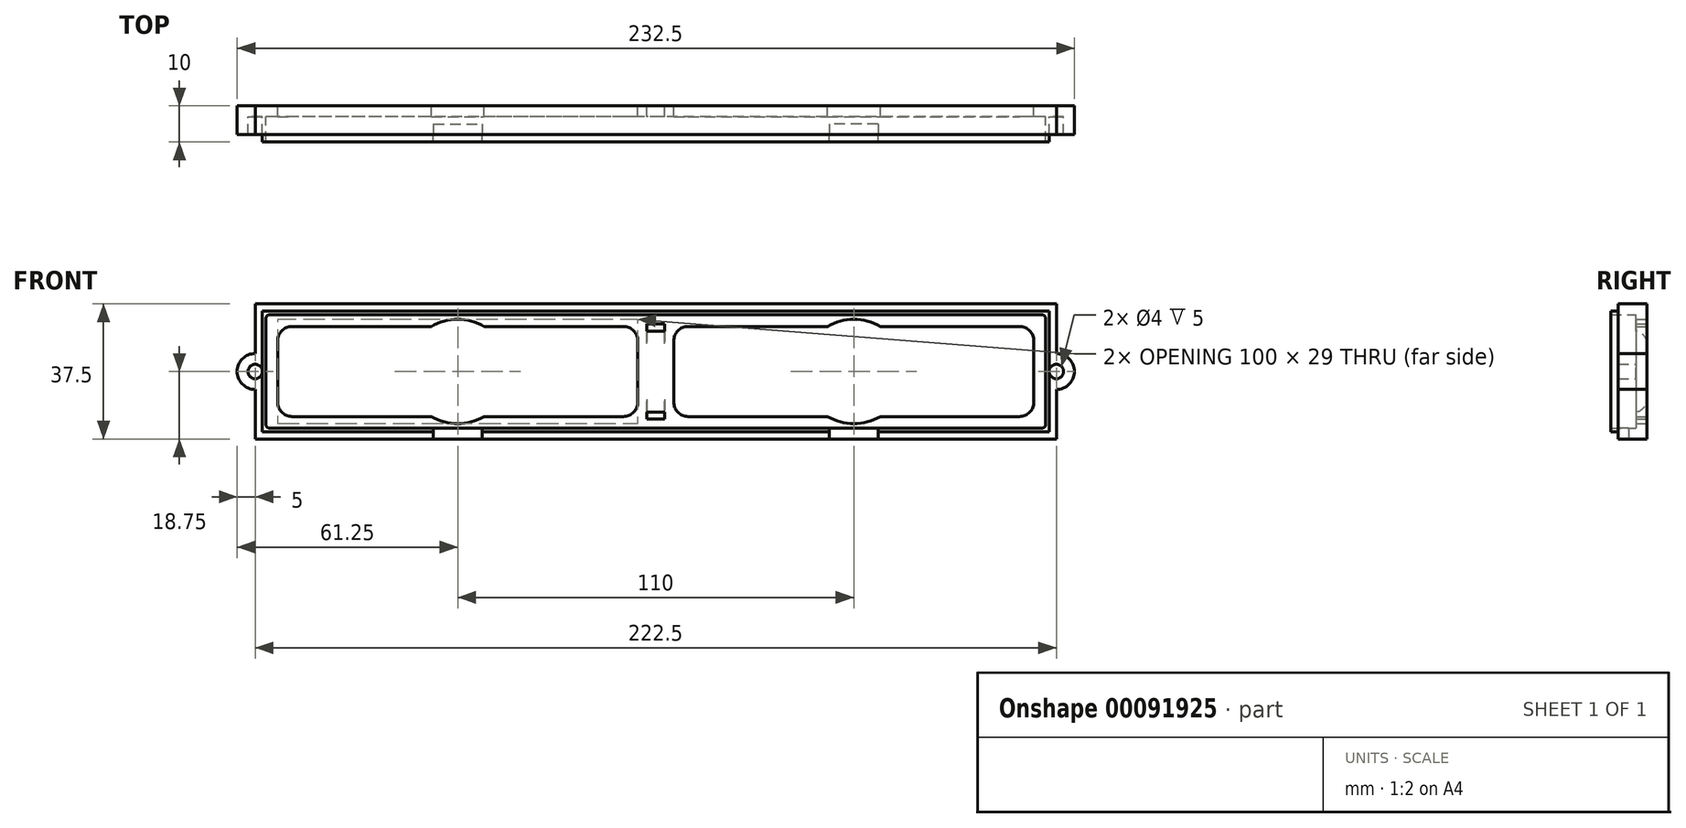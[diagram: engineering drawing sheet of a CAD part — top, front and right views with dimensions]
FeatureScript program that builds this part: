
annotation { "Feature Type Name" : "Feature", "Feature Type Description" : "" }
export const myFeature = defineFeature(function(context is Context, id is Id, definition is map)
    precondition{}
    {
        {
            var Q0;
            Q0=qCreatedBy(makeId("Front.planeOp"),FACE);
            var sketch = newSketch(context, id + "F0", { "sketchPlane" : qUnion([Q0])});
            skLineSegment(sketch, "E0.bottom", {"start": v(111.25, 18.75) * mm, "end": v(-111.25, 18.75) * mm});
            skLineSegment(sketch, "E0.top", {"start": v(111.25, -18.75) * mm, "end": v(-111.25, -18.75) * mm});
            skLineSegment(sketch, "E0.left", {"start": v(111.25, 18.75) * mm, "end": v(111.25, -18.75) * mm});
            skLineSegment(sketch, "E0.right", {"start": v(-111.25, 18.75) * mm, "end": v(-111.25, -18.75) * mm});
            skPoint(sketch, "E0.middle", {"position": v(0, 0) * mm});
            skLineSegment(sketch, "E1.bottom", {"start": v(-9, 12.5) * mm, "end": v(-101, 12.5) * mm});
            skLineSegment(sketch, "E1.top", {"start": v(-9, -12.5) * mm, "end": v(-101, -12.5) * mm});
            skLineSegment(sketch, "E1.left", {"start": v(-5, 8.5) * mm, "end": v(-5, -8.5) * mm});
            skLineSegment(sketch, "E1.right", {"start": v(-105, 8.5) * mm, "end": v(-105, -8.5) * mm});
            skPoint(sketch, "E1.middle", {"position": v(-55, 0) * mm});
            skPoint(sketch, "E2.visualSharp", {"position": v(-105, 12.5) * mm});
            skArc(sketch, "E2.filletArc", {"start": v(-101, 12.5) * mm, "mid": v(-103.83, 11.33) * mm, "end": v(-105, 8.5) * mm});
            skPoint(sketch, "E3.visualSharp", {"position": v(-5, 12.5) * mm});
            skArc(sketch, "E3.filletArc", {"start": v(-5, 8.5) * mm, "mid": v(-6.17, 11.33) * mm, "end": v(-9, 12.5) * mm});
            skPoint(sketch, "E4.visualSharp", {"position": v(-5, -12.5) * mm});
            skArc(sketch, "E4.filletArc", {"start": v(-9, -12.5) * mm, "mid": v(-6.17, -11.33) * mm, "end": v(-5, -8.5) * mm});
            skPoint(sketch, "E5.visualSharp", {"position": v(-105, -12.5) * mm});
            skArc(sketch, "E5.filletArc", {"start": v(-105, -8.5) * mm, "mid": v(-103.83, -11.33) * mm, "end": v(-101, -12.5) * mm});
            skArc(sketch, "E6.MirrorCS", {"start": v(101, 12.5) * mm, "mid": v(103.83, 11.33) * mm, "end": v(105, 8.5) * mm});
            skArc(sketch, "E7.MirrorCS", {"start": v(5, 8.5) * mm, "mid": v(6.17, 11.33) * mm, "end": v(9, 12.5) * mm});
            skArc(sketch, "E8.MirrorCS", {"start": v(9, -12.5) * mm, "mid": v(6.17, -11.33) * mm, "end": v(5, -8.5) * mm});
            skArc(sketch, "E9.MirrorCS", {"start": v(105, -8.5) * mm, "mid": v(103.83, -11.33) * mm, "end": v(101, -12.5) * mm});
            skLineSegment(sketch, "E10.MirrorCS", {"start": v(9, -12.5) * mm, "end": v(101, -12.5) * mm});
            skPoint(sketch, "E11.MirrorP", {"position": v(105, -12.5) * mm});
            skLineSegment(sketch, "E12.MirrorCS", {"start": v(5, 8.5) * mm, "end": v(5, -8.5) * mm});
            skLineSegment(sketch, "E13.MirrorCS", {"start": v(9, 12.5) * mm, "end": v(101, 12.5) * mm});
            skLineSegment(sketch, "E14.MirrorCS", {"start": v(105, 8.5) * mm, "end": v(105, -8.5) * mm});
            skPoint(sketch, "E15.MirrorP", {"position": v(5, 12.5) * mm});
            skPoint(sketch, "E16.MirrorP", {"position": v(105, 12.5) * mm});
            skPoint(sketch, "E17.MirrorP", {"position": v(55, 0) * mm});
            skPoint(sketch, "E18.MirrorP", {"position": v(5, -12.5) * mm});
            skCircle(sketch, "E19", {"center": v(-55, 0) * mm, "radius": 14.5 * mm});
            skCircle(sketch, "E20.MirrorC", {"center": v(55, 0) * mm, "radius": 14.5 * mm});
            skArc(sketch, "E21", {"start": v(-111.25, -5) * mm, "mid": v(-116.25, 0) * mm, "end": v(-111.25, 5) * mm});
            skArc(sketch, "E22.MirrorCS", {"start": v(111.25, -5) * mm, "mid": v(116.25, 0) * mm, "end": v(111.25, 5) * mm});
            skLineSegment(sketch, "E23.bottom", {"start": v(2.5, 11.25) * mm, "end": v(-2.5, 11.25) * mm});
            skLineSegment(sketch, "E23.top", {"start": v(2.5, 13.25) * mm, "end": v(-2.5, 13.25) * mm});
            skLineSegment(sketch, "E23.left", {"start": v(2.5, 11.25) * mm, "end": v(2.5, 13.25) * mm});
            skLineSegment(sketch, "E23.right", {"start": v(-2.5, 11.25) * mm, "end": v(-2.5, 13.25) * mm});
            skPoint(sketch, "E23.middle", {"position": v(0, 12.25) * mm});
            skLineSegment(sketch, "E24.MirrorCS", {"start": v(-2.5, -11.25) * mm, "end": v(-2.5, -13.25) * mm});
            skLineSegment(sketch, "E25.MirrorCS", {"start": v(2.5, -11.25) * mm, "end": v(-2.5, -11.25) * mm});
            skPoint(sketch, "E26.MirrorP", {"position": v(0, -12.25) * mm});
            skLineSegment(sketch, "E27.MirrorCS", {"start": v(2.5, -11.25) * mm, "end": v(2.5, -13.25) * mm});
            skLineSegment(sketch, "E28.MirrorCS", {"start": v(2.5, -13.25) * mm, "end": v(-2.5, -13.25) * mm});
            skSolve(sketch);
        }
        {
            var Q0;
            Q0 = qSketchRegion(id + "F0", true);
            extrude(context, id + "F1", {"entities" : qUnion([Q0]), "depth" : 3 * mm});
        }
        {
            var Q0;
            Q0=makeQuery(id+"F1.opExtrude","CAP_FACE",FACE,{"disambiguationData":[OSD([sQuery(id+"F0.wireOp",EDGE,"E0.bottom"),sQuery(id+"F0.wireOp",EDGE,"E0.top"),sQuery(id+"F0.wireOp",EDGE,"E0.left"),sQuery(id+"F0.wireOp",EDGE,"E0.right"),sQuery(id+"F0.wireOp",EDGE,"E1.bottom"),sQuery(id+"F0.wireOp",EDGE,"E1.top"),sQuery(id+"F0.wireOp",EDGE,"E1.left"),sQuery(id+"F0.wireOp",EDGE,"E1.right"),sQuery(id+"F0.wireOp",EDGE,"E2.filletArc"),sQuery(id+"F0.wireOp",EDGE,"E3.filletArc"),sQuery(id+"F0.wireOp",EDGE,"E4.filletArc"),sQuery(id+"F0.wireOp",EDGE,"E5.filletArc"),sQuery(id+"F0.wireOp",EDGE,"E6.MirrorCS"),sQuery(id+"F0.wireOp",EDGE,"E7.MirrorCS"),sQuery(id+"F0.wireOp",EDGE,"E8.MirrorCS"),sQuery(id+"F0.wireOp",EDGE,"E9.MirrorCS"),sQuery(id+"F0.wireOp",EDGE,"E10.MirrorCS"),sQuery(id+"F0.wireOp",EDGE,"E12.MirrorCS"),sQuery(id+"F0.wireOp",EDGE,"E13.MirrorCS"),sQuery(id+"F0.wireOp",EDGE,"E14.MirrorCS")])],"isStart":false});
            var sketch = newSketch(context, id + "F2", { "sketchPlane" : qUnion([Q0])});
            skLineSegment(sketch, "E29.bottom", {"start": v(107.25, 15.75) * mm, "end": v(-107.25, 15.75) * mm});
            skLineSegment(sketch, "E29.top", {"start": v(107.25, -15.75) * mm, "end": v(-107.25, -15.75) * mm});
            skLineSegment(sketch, "E29.left", {"start": v(108.25, 14.75) * mm, "end": v(108.25, -14.75) * mm});
            skLineSegment(sketch, "E29.right", {"start": v(-108.25, 14.75) * mm, "end": v(-108.25, -14.75) * mm});
            skPoint(sketch, "E30.visualSharp", {"position": v(-108.25, 15.75) * mm});
            skArc(sketch, "E30.filletArc", {"start": v(-107.25, 15.75) * mm, "mid": v(-107.96, 15.46) * mm, "end": v(-108.25, 14.75) * mm});
            skPoint(sketch, "E31.visualSharp", {"position": v(108.25, 15.75) * mm});
            skArc(sketch, "E31.filletArc", {"start": v(108.25, 14.75) * mm, "mid": v(107.96, 15.46) * mm, "end": v(107.25, 15.75) * mm});
            skPoint(sketch, "E32.visualSharp", {"position": v(108.25, -15.75) * mm});
            skArc(sketch, "E32.filletArc", {"start": v(107.25, -15.75) * mm, "mid": v(107.96, -15.46) * mm, "end": v(108.25, -14.75) * mm});
            skPoint(sketch, "E33.visualSharp", {"position": v(-108.25, -15.75) * mm});
            skArc(sketch, "E33.filletArc", {"start": v(-108.25, -14.75) * mm, "mid": v(-107.96, -15.46) * mm, "end": v(-107.25, -15.75) * mm});
            skCircle(sketch, "E34", {"center": v(-111.25, 0) * mm, "radius": 2 * mm});
            skCircle(sketch, "E35.MirrorC", {"center": v(111.25, 0) * mm, "radius": 2 * mm});
            skSolve(sketch);
        }
        {
            var Q0;
            Q0=makeQuery(id+"F2.imprint","IMPRINT",FACE,{"disambiguationData":[TD([[makeQuery(id+"F2.imprint","IMPRINT",EDGE,{"derivedFrom":sQuery(id+"F2.wireOp",EDGE,"E29.bottom")}),-1.0]])]});
            var Q1;
            Q1=makeQuery(id+"F2.imprint","IMPRINT",FACE,{"disambiguationData":[TD([[makeQuery(id+"F2.imprint","IMPRINT",EDGE,{"derivedFrom":sQuery(id+"F2.wireOp",EDGE,"8UQ35Aj4-GzFw-aaHB-QqC8-tIVl76PQ1ExV")}),1.0]])]});
            extrude(context, id + "F3", {"entities" : qUnion([Q0, Q1]), "operationType" : NewBodyOperationType.ADD, "depth" : 5 * mm});
        }
        {
            var Q0;
            Q0=makeQuery(id+"F3.opExtrude","CAP_FACE",FACE,{"disambiguationData":[OSD([sQuery(id+"F0.wireOp",EDGE,"E0.bottom"),sQuery(id+"F0.wireOp",EDGE,"E0.top"),sQuery(id+"F0.wireOp",EDGE,"E0.left"),sQuery(id+"F0.wireOp",EDGE,"E0.right"),sQuery(id+"F0.wireOp",EDGE,"E21"),sQuery(id+"F0.wireOp",EDGE,"E22.MirrorCS"),sQuery(id+"F2.wireOp",EDGE,"E29.bottom"),sQuery(id+"F2.wireOp",EDGE,"E29.top"),sQuery(id+"F2.wireOp",EDGE,"E29.left"),sQuery(id+"F2.wireOp",EDGE,"E29.right"),sQuery(id+"F2.wireOp",EDGE,"E30.filletArc"),sQuery(id+"F2.wireOp",EDGE,"E31.filletArc"),sQuery(id+"F2.wireOp",EDGE,"E32.filletArc"),sQuery(id+"F2.wireOp",EDGE,"E33.filletArc"),sQuery(id+"F2.wireOp",EDGE,"E34"),sQuery(id+"F2.wireOp",EDGE,"E35.MirrorC")])],"isStart":false});
            var sketch = newSketch(context, id + "F4", { "sketchPlane" : qUnion([Q0])});
            skLineSegment(sketch, "E36.bottom", {"start": v(-109.25, 16.75) * mm, "end": v(109.25, 16.75) * mm});
            skLineSegment(sketch, "E36.top", {"start": v(-109.25, -16.75) * mm, "end": v(109.25, -16.75) * mm});
            skLineSegment(sketch, "E36.left", {"start": v(-109.25, 16.75) * mm, "end": v(-109.25, -16.75) * mm});
            skLineSegment(sketch, "E36.right", {"start": v(109.25, 16.75) * mm, "end": v(109.25, -16.75) * mm});
            skPoint(sketch, "E36.middle", {"position": v(0, 0) * mm});
            skLineSegment(sketch, "E37.bottom", {"start": v(-107.25, 15.75) * mm, "end": v(107.25, 15.75) * mm});
            skLineSegment(sketch, "E37.top", {"start": v(-107.25, -15.75) * mm, "end": v(107.25, -15.75) * mm});
            skLineSegment(sketch, "E37.left", {"start": v(-108.25, 14.75) * mm, "end": v(-108.25, -14.75) * mm});
            skLineSegment(sketch, "E37.right", {"start": v(108.25, 14.75) * mm, "end": v(108.25, -14.75) * mm});
            skPoint(sketch, "E38.visualSharp", {"position": v(-108.25, 15.75) * mm});
            skArc(sketch, "E38.filletArc", {"start": v(-107.25, 15.75) * mm, "mid": v(-107.96, 15.46) * mm, "end": v(-108.25, 14.75) * mm});
            skPoint(sketch, "E39.visualSharp", {"position": v(-108.25, -15.75) * mm});
            skArc(sketch, "E39.filletArc", {"start": v(-108.25, -14.75) * mm, "mid": v(-107.96, -15.46) * mm, "end": v(-107.25, -15.75) * mm});
            skPoint(sketch, "E40.visualSharp", {"position": v(108.25, 15.75) * mm});
            skArc(sketch, "E40.filletArc", {"start": v(108.25, 14.75) * mm, "mid": v(107.96, 15.46) * mm, "end": v(107.25, 15.75) * mm});
            skPoint(sketch, "E41.visualSharp", {"position": v(108.25, -15.75) * mm});
            skArc(sketch, "E41.filletArc", {"start": v(107.25, -15.75) * mm, "mid": v(107.96, -15.46) * mm, "end": v(108.25, -14.75) * mm});
            skSolve(sketch);
        }
        {
            var Q0;
            Q0 = qSketchRegion(id + "F4", true);
            extrude(context, id + "F5", {"entities" : qUnion([Q0]), "operationType" : NewBodyOperationType.ADD, "depth" : 2 * mm});
        }
        {
            var Q0;
            {var subQ0=sQuery(id+"F0.wireOp",EDGE,"E0.top");Q0=makeQuery(id+"F3.boolean.opBoolean","MERGE",FACE,{"derivedFrom":[makeQuery(id+"F1.opExtrude","SWEPT_FACE",FACE,{"disambiguationData":[OSD([subQ0])]}),makeQuery(id+"F3.opExtrude","SWEPT_FACE",FACE,{"disambiguationData":[OSD([subQ0])]})]});}
            var sketch = newSketch(context, id + "F6", { "sketchPlane" : qUnion([Q0])});
            skLineSegment(sketch, "E42.bottom", {"start": v(-61.75, 5) * mm, "end": v(-48.25, 5) * mm});
            skLineSegment(sketch, "E42.top", {"start": v(-61.75, 10) * mm, "end": v(-48.25, 10) * mm});
            skLineSegment(sketch, "E42.left", {"start": v(-61.75, 5) * mm, "end": v(-61.75, 10) * mm});
            skLineSegment(sketch, "E42.right", {"start": v(-48.25, 5) * mm, "end": v(-48.25, 10) * mm});
            skPoint(sketch, "E43", {"position": v(-55, 5) * mm});
            skPoint(sketch, "E44.MirrorP", {"position": v(55, 5) * mm});
            skLineSegment(sketch, "E45.MirrorCS", {"start": v(48.25, 5) * mm, "end": v(48.25, 10) * mm});
            skLineSegment(sketch, "E46.MirrorCS", {"start": v(61.75, 5) * mm, "end": v(61.75, 10) * mm});
            skLineSegment(sketch, "E47.MirrorCS", {"start": v(61.75, 5) * mm, "end": v(48.25, 5) * mm});
            skLineSegment(sketch, "E48.MirrorCS", {"start": v(61.75, 10) * mm, "end": v(48.25, 10) * mm});
            skSolve(sketch);
        }
        {
            var Q0;
            Q0 = qSketchRegion(id + "F6", true);
            extrude(context, id + "F7", {"entities" : qUnion([Q0]), "operationType" : NewBodyOperationType.REMOVE, "oppositeDirection" : true, "depth" : 25 * mm});
        }
        {
            var Q0;
            Q0=makeQuery(id+"F1.opExtrude","CAP_EDGE",EDGE,{"disambiguationData":[OSD([sQuery(id+"F0.wireOp",EDGE,"E23.bottom")])],"isStart":true});
            var Q1;
            Q1=makeQuery(id+"F1.opExtrude","CAP_EDGE",EDGE,{"disambiguationData":[OSD([sQuery(id+"F0.wireOp",EDGE,"E25.MirrorCS")])],"isStart":true});
            fillet(context, id + "F8", {"entities" : qUnion([Q0, Q1]), "radius" : 3.5 * mm, "tangentPropagation" : true, "allowEdgeOverflow" : false});
        }
    });
